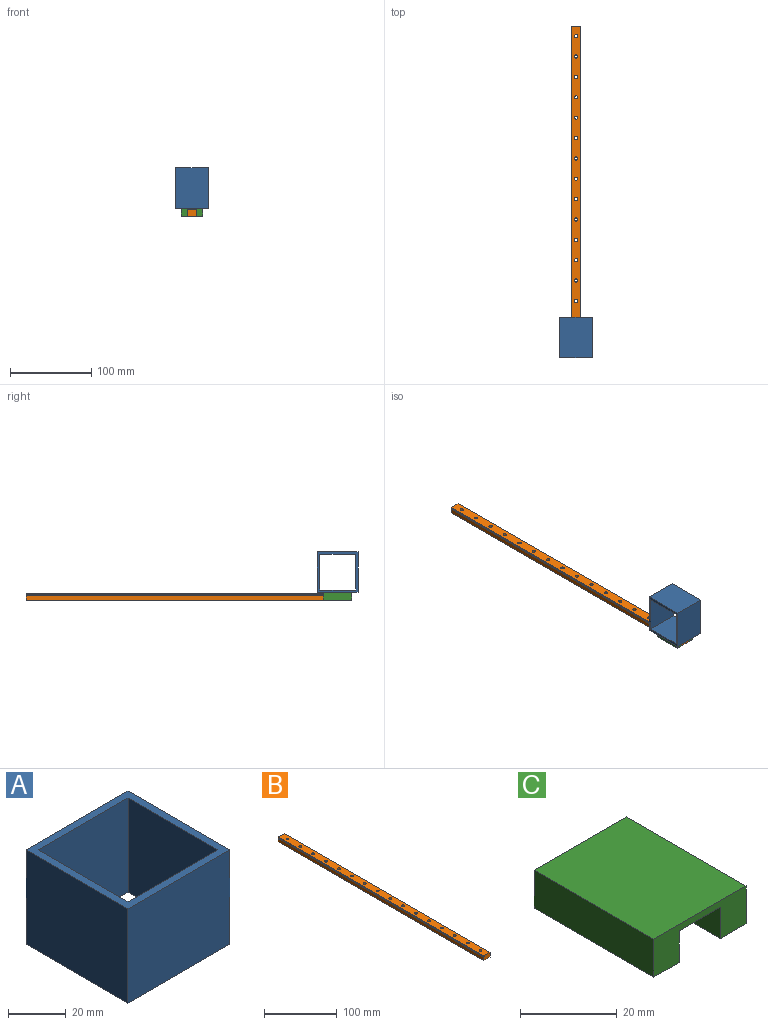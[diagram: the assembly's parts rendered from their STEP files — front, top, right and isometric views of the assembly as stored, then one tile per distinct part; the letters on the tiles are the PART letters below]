
ASSEMBLY  parts=3 mates=2
PART A: 10 faces, bbox 50x50x40 mm
  f0: plane 50x40mm, normal (0,-1,0), area 2000mm2, adj f1,f7,f8,f9
  f1: plane 50x40mm, normal (1,0,0), area 2000mm2, adj f0,f2,f8,f9
  f2: plane 50x40mm, normal (0,1,0), area 2000mm2, adj f1,f7,f8,f9
  f3: plane 44x40mm, normal (0,1,0), area 1760mm2, adj f4,f6,f8,f9
  f4: plane 44x40mm, normal (1,0,0), area 1760mm2, adj f3,f5,f8,f9
  f5: plane 44x40mm, normal (0,-1,0), area 1760mm2, adj f4,f6,f8,f9
  f6: plane 44x40mm, normal (-1,0,0), area 1760mm2, adj f3,f5,f8,f9
  f7: plane 50x40mm, normal (-1,0,0), area 2000mm2, adj f0,f2,f8,f9
  f8: plane 50x50mm, normal (0,0,1), area 564mm2, adj f0,f1,f2,f3,f4,f5,f6,f7
  f9: plane 50x50mm, normal (0,0,-1), area 564mm2, adj f0,f1,f2,f3,f4,f5,f6,f7
PART B: 28 faces, bbox 12x400x8 mm
  f0: plane 400x12mm, normal (0,0,1), area 4598.9mm2, adj f1,f9,f10,f11,f12,f13,f14,f15
  f1: plane 400x1.5mm, normal (-1,0,0), area 600mm2, adj f0,f2,f10,f11
  f2: plane 400x0.5mm, normal (-0.71,0,-0.71), area 282.8mm2, adj f1,f3,f10,f11
  f3: plane 400x0.5mm, normal (-0.71,0,0.71), area 282.8mm2, adj f2,f4,f10,f11
  f4: plane 400x5.5mm, normal (-1,0,0), area 2200mm2, adj f3,f5,f10,f11
  f5: plane 400x12mm, normal (0,0,-1), area 4598.9mm2, adj f4,f6,f10,f11,f12,f13,f14,f15
  f6: plane 400x5.5mm, normal (1,0,0), area 2200mm2, adj f5,f7,f10,f11
  f7: plane 400x0.5mm, normal (0.71,0,0.71), area 282.8mm2, adj f6,f8,f10,f11
  f8: plane 400x0.5mm, normal (0.71,0,-0.71), area 282.8mm2, adj f7,f9,f10,f11
  f9: plane 400x1.5mm, normal (1,0,0), area 600mm2, adj f0,f8,f10,f11
  f10: plane 12x8mm, normal (0,-1,0), area 95.5mm2, adj f0,f1,f2,f3,f4,f5,f6,f7
  f11: plane 12x8mm, normal (0,1,0), area 95.5mm2, adj f0,f1,f2,f3,f4,f5,f6,f7
  f12: cylinder r=2mm len=8mm, axis (0,0,1), area 100.5mm2, adj f0,f5
  f13: cylinder r=2mm len=8mm, axis (0,0,1), area 100.5mm2, adj f0,f5
  f14: cylinder r=2mm len=8mm, axis (0,0,1), area 100.5mm2, adj f0,f5
  f15: cylinder r=2mm len=8mm, axis (0,0,1), area 100.5mm2, adj f0,f5
  f16: cylinder r=2mm len=8mm, axis (0,0,1), area 100.5mm2, adj f0,f5
  f17: cylinder r=2mm len=8mm, axis (0,0,1), area 100.5mm2, adj f0,f5
  f18: cylinder r=2mm len=8mm, axis (0,0,1), area 100.5mm2, adj f0,f5
  f19: cylinder r=2mm len=8mm, axis (0,0,1), area 100.5mm2, adj f0,f5
  f20: cylinder r=2mm len=8mm, axis (0,0,1), area 100.5mm2, adj f0,f5
  f21: cylinder r=2mm len=8mm, axis (0,0,1), area 100.5mm2, adj f0,f5
  f22: cylinder r=2mm len=8mm, axis (0,0,1), area 100.5mm2, adj f0,f5
  f23: cylinder r=2mm len=8mm, axis (0,0,1), area 100.5mm2, adj f0,f5
  f24: cylinder r=2mm len=8mm, axis (0,0,1), area 100.5mm2, adj f0,f5
  f25: cylinder r=2mm len=8mm, axis (0,0,1), area 100.5mm2, adj f0,f5
  f26: cylinder r=2mm len=8mm, axis (0,0,1), area 100.5mm2, adj f0,f5
  f27: cylinder r=2mm len=8mm, axis (0,0,1), area 100.5mm2, adj f0,f5
PART C: 10 faces, bbox 27x35x9.6 mm
  f0: plane 35x7.5mm, normal (0,0,-1), area 262.5mm2, adj f1,f7,f8,f9
  f1: plane 35x8mm, normal (1,0,0), area 280mm2, adj f0,f2,f8,f9
  f2: plane 35x12mm, normal (0,0,-1), area 420mm2, adj f1,f3,f8,f9
  f3: plane 35x8mm, normal (-1,0,0), area 280mm2, adj f2,f4,f8,f9
  f4: plane 35x7.5mm, normal (0,0,-1), area 262.5mm2, adj f3,f5,f8,f9
  f5: plane 35x9.6mm, normal (1,0,0), area 336mm2, adj f4,f6,f8,f9
  f6: plane 35x27mm, normal (0,0,1), area 945mm2, adj f5,f7,f8,f9
  f7: plane 35x9.6mm, normal (-1,0,0), area 336mm2, adj f0,f6,f8,f9
  f8: plane 27x9.6mm, normal (0,-1,0), area 163.2mm2, adj f0,f1,f2,f3,f4,f5,f6,f7
  f9: plane 27x9.6mm, normal (0,1,0), area 163.2mm2, adj f0,f1,f2,f3,f4,f5,f6,f7
PLACE A rot(axis=(0.58,0.58,0.58),120deg) t=(52.07,-79.5,122.69)mm
PLACE B t=(72.07,303,88.09)mm fixed
PLACE C t=(72.07,338,88.09)mm
MATE slider C.f8 <-> B.f10  axis (0,-1,0) through (66.07,-97,96.09)mm
MATE fastened C.f6 <-> A.f0  axis (0,0,1) through (72.07,-79.5,97.69)mm
